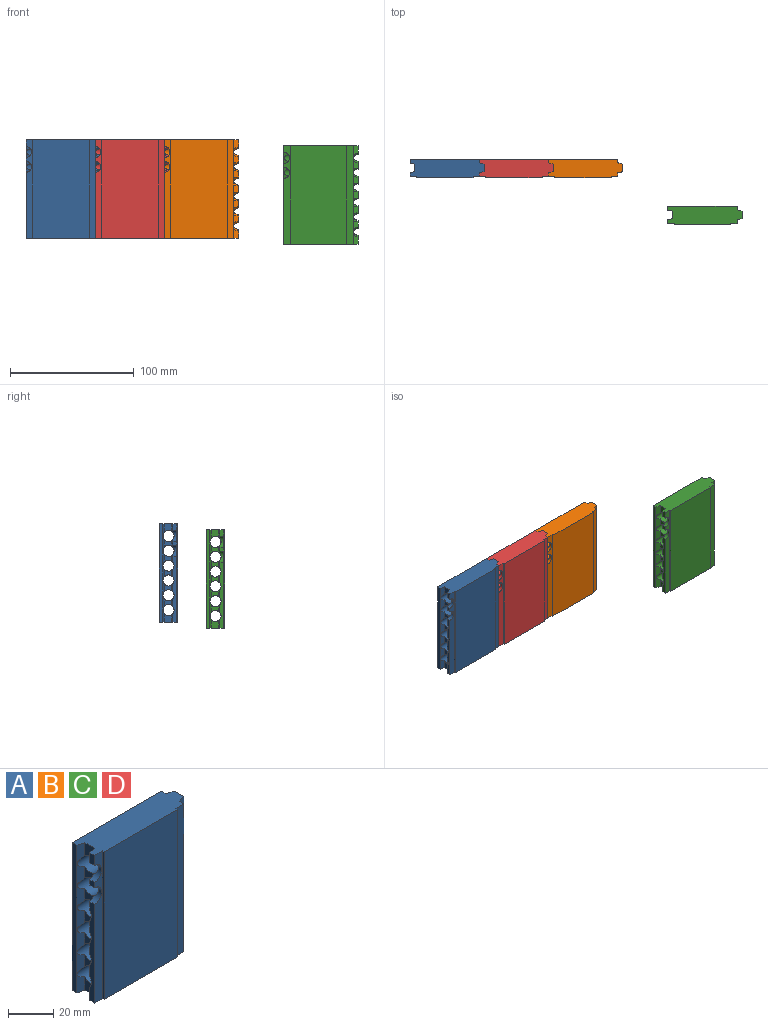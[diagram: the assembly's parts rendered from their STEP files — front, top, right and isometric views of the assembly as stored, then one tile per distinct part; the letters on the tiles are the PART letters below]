
ASSEMBLY  parts=4 mates=2
PART A: 64 faces, bbox 60x15x80 mm
  f0: plane 5.5x3mm, normal (-1,0,0), area 16.5mm2, adj f2,f34,f54,f62
  f1: plane 3x3mm, normal (-1,0,0), area 9mm2, adj f2,f35,f62,f63
  f2: plane 80x5mm, normal (0,-1,0), area 336.4mm2, adj f0,f1,f40,f53,f54,f55,f62,f63
  f3: plane 6.34x4mm, normal (0.24,-0.97,0), area 22mm2, adj f10,f44,f60,f61
  f4: plane 6.34x4mm, normal (0.24,-0.97,0), area 22mm2, adj f11,f44,f59,f60
  f5: plane 6.34x4mm, normal (0.24,-0.97,0), area 22mm2, adj f12,f44,f58,f59
  f6: plane 6.34x4mm, normal (0.24,-0.97,0), area 22mm2, adj f13,f44,f57,f58
  f7: plane 6.34x4mm, normal (0.24,-0.97,0), area 22mm2, adj f14,f44,f56,f57
  f8: plane 7.17x4mm, normal (0.24,-0.97,0), area 27.5mm2, adj f15,f44,f55,f56
  f9: plane 7.17x6mm, normal (1,0,0), area 35.4mm2, adj f16,f45,f54,f61
  f10: plane 6.34x6mm, normal (1,0,0), area 22.8mm2, adj f3,f17,f60,f61
  f11: plane 6.34x6mm, normal (1,0,0), area 22.8mm2, adj f4,f18,f59,f60
  f12: plane 6.34x6mm, normal (1,0,0), area 22.8mm2, adj f5,f19,f58,f59
  f13: plane 6.34x6mm, normal (1,0,0), area 22.8mm2, adj f6,f20,f57,f58
  f14: plane 6.34x6mm, normal (1,0,0), area 22.8mm2, adj f7,f21,f56,f57
  f15: plane 7.17x6mm, normal (1,0,0), area 35.4mm2, adj f8,f46,f55,f56
  f16: plane 10x4mm, normal (0.24,0.97,0), area 33.3mm2, adj f9,f47,f54,f61
  f17: plane 12x4mm, normal (0.24,0.97,0), area 33.5mm2, adj f10,f47,f60,f61
  f18: plane 12x4mm, normal (0.24,0.97,0), area 33.5mm2, adj f11,f47,f59,f60
  f19: plane 12x4mm, normal (0.24,0.97,0), area 33.5mm2, adj f12,f47,f58,f59
  f20: plane 12x4mm, normal (0.24,0.97,0), area 33.5mm2, adj f13,f47,f57,f58
  f21: plane 12x4mm, normal (0.24,0.97,0), area 33.5mm2, adj f14,f47,f56,f57
  f22: plane 12x4mm, normal (-0.24,-0.97,0), area 33.5mm2, adj f29,f49,f60,f61
  f23: plane 12x4mm, normal (-0.24,-0.97,0), area 33.5mm2, adj f30,f49,f59,f60
  f24: plane 12x4mm, normal (-0.24,-0.97,0), area 33.5mm2, adj f31,f49,f58,f59
  f25: plane 12x4mm, normal (-0.24,-0.97,0), area 33.5mm2, adj f32,f49,f57,f58
  f26: plane 12x4mm, normal (-0.24,-0.97,0), area 33.5mm2, adj f33,f49,f56,f57
  f27: plane 10x4mm, normal (-0.24,-0.97,0), area 33.3mm2, adj f49,f51,f55,f56
  f28: plane 7.17x6mm, normal (-1,0,0), area 35.4mm2, adj f34,f50,f54,f61
  f29: plane 6.34x6mm, normal (-1,0,0), area 22.8mm2, adj f22,f35,f60,f61
  f30: plane 6.34x6mm, normal (-1,0,0), area 22.8mm2, adj f23,f36,f59,f60
  f31: plane 6.34x6mm, normal (-1,0,0), area 22.8mm2, adj f24,f37,f58,f59
  f32: plane 6.34x6mm, normal (-1,0,0), area 22.8mm2, adj f25,f38,f57,f58
  f33: plane 6.34x6mm, normal (-1,0,0), area 22.8mm2, adj f26,f39,f56,f57
  f34: plane 6.5x4.02mm, normal (-0.24,0.97,0), area 24.6mm2, adj f0,f28,f54,f61,f62
  f35: plane 4.97x4.02mm, normal (-0.24,0.97,0), area 16.3mm2, adj f1,f29,f60,f61,f62,f63
  f36: plane 5.67x4.02mm, normal (-0.24,0.97,0), area 19.2mm2, adj f30,f40,f59,f60,f63
  f37: plane 6.34x4mm, normal (-0.24,0.97,0), area 22mm2, adj f31,f40,f58,f59
  f38: plane 6.34x4mm, normal (-0.24,0.97,0), area 22mm2, adj f32,f40,f57,f58
  f39: plane 6.34x4mm, normal (-0.24,0.97,0), area 22mm2, adj f33,f40,f56,f57
  f40: plane 53.5x3mm, normal (-1,0,0), area 145mm2, adj f2,f36,f37,f38,f39,f52,f55,f56
  f41: plane 80x46mm, normal (0,-1,0), area 3680mm2, adj f42,f53,f54,f55
  f42: plane 80x1mm, normal (1,0,0), area 80mm2, adj f41,f43,f54,f55
  f43: plane 80x5mm, normal (0,-1,0), area 400mm2, adj f42,f44,f54,f55
  f44: plane 80x3mm, normal (1,0,0), area 216.8mm2, adj f3,f4,f5,f6,f7,f8,f43,f45
  f45: plane 7.17x4mm, normal (0.24,-0.97,0), area 27.5mm2, adj f9,f44,f54,f61
  f46: plane 10x4mm, normal (0.24,0.97,0), area 33.3mm2, adj f15,f47,f55,f56
  f47: plane 80x3mm, normal (1,0,0), area 240mm2, adj f16,f17,f18,f19,f20,f21,f46,f48
  f48: plane 80x56mm, normal (0,1,0), area 4480mm2, adj f47,f49,f54,f55
  f49: plane 80x3mm, normal (-1,0,0), area 240mm2, adj f22,f23,f24,f25,f26,f27,f48,f50
  f50: plane 10x4mm, normal (-0.24,-0.97,0), area 33.3mm2, adj f28,f49,f54,f61
  f51: plane 7.17x6mm, normal (-1,0,0), area 35.4mm2, adj f27,f52,f55,f56
  f52: plane 7.17x4mm, normal (-0.24,0.97,0), area 27.5mm2, adj f40,f51,f55,f56
  f53: plane 80x1mm, normal (-1,0,0), area 80mm2, adj f2,f41,f54,f55
  f54: plane 60x15mm, normal (0,0,1), area 830mm2, adj f0,f2,f9,f16,f28,f34,f41,f42
  f55: plane 60x15mm, normal (0,0,-1), area 830mm2, adj f2,f8,f15,f27,f40,f41,f42,f43
  f56: cylinder r=4.5mm len=60mm, axis (1,0,0), area 1583.4mm2, adj f7,f8,f14,f15,f21,f26,f27,f33
  f57: cylinder r=4.5mm len=60mm, axis (1,0,0), area 1583.4mm2, adj f6,f7,f13,f14,f20,f21,f25,f26
  f58: cylinder r=4.5mm len=60mm, axis (1,0,0), area 1583.4mm2, adj f5,f6,f12,f13,f19,f20,f24,f25
  f59: cylinder r=4.5mm len=60mm, axis (1,0,0), area 1583.4mm2, adj f4,f5,f11,f12,f18,f19,f23,f24
  f60: cylinder r=4.5mm len=60mm, axis (1,0,0), area 1554.3mm2, adj f3,f4,f10,f11,f17,f18,f22,f23
  f61: cylinder r=4.5mm len=60mm, axis (1,0,0), area 1554.3mm2, adj f3,f9,f10,f16,f17,f22,f28,f29
  f62: cylinder r=4.5mm len=9mm, axis (0,-1,0), area 41.2mm2, adj f0,f1,f2,f34,f35,f61
  f63: cylinder r=4.5mm len=9mm, axis (0,-1,0), area 41.2mm2, adj f1,f2,f35,f36,f40,f60
PART B: same geometry as A
PART C: same geometry as A
PART D: same geometry as A
PLACE A t=(-91.03,-10.58,-34.03)mm
PLACE B t=(20.97,-10.58,-34.03)mm
PLACE C t=(117.68,-48.6,-38.83)mm
PLACE D t=(-35.03,-10.58,-34.03)mm
MATE fastened D.f51 <-> A.f15  axis (-1,0,0) through (-61.03,-2.51,-31.07)mm
MATE fastened D.f15 <-> B.f51  axis (1,0,0) through (-5.03,-2.51,-31.07)mm
